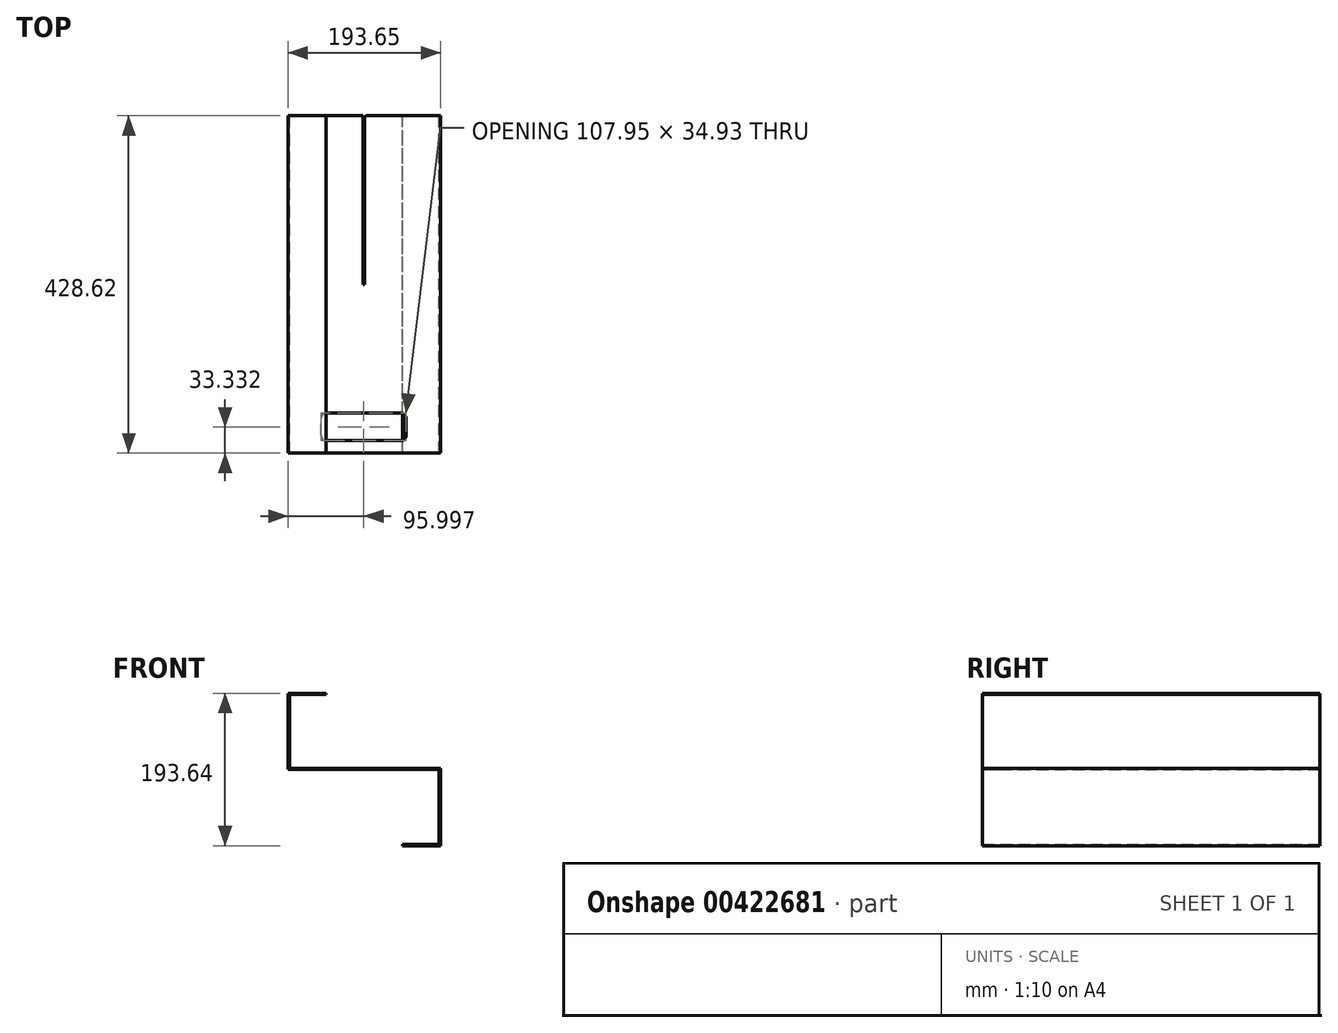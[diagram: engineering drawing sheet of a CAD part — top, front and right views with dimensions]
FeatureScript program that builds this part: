
annotation { "Feature Type Name" : "Feature", "Feature Type Description" : "" }
export const myFeature = defineFeature(function(context is Context, id is Id, definition is map)
    precondition{}
    {
        {
            var Q0;
            Q0=qCreatedBy(makeId("Front.planeOp"),FACE);
            var sketch = newSketch(context, id + "F0", { "sketchPlane" : qUnion([Q0])});
            skLineSegment(sketch, "E0", {"start": v(0, 96.82) * mm, "end": v(-48.41, 96.82) * mm});
            skLineSegment(sketch, "E1", {"start": v(-48.41, 96.82) * mm, "end": v(-48.41, 0) * mm});
            skLineSegment(sketch, "E2", {"start": v(-48.41, 0) * mm, "end": v(143.59, 0) * mm});
            skLineSegment(sketch, "E3", {"start": v(145.24, 1.65) * mm, "end": v(145.24, -96.82) * mm});
            skLineSegment(sketch, "E4", {"start": v(145.24, -96.82) * mm, "end": v(96.82, -96.82) * mm});
            skLineSegment(sketch, "E5.0", {"start": v(0, 95.17) * mm, "end": v(-46.76, 95.17) * mm});
            skLineSegment(sketch, "E6.0", {"start": v(-46.76, 95.17) * mm, "end": v(-46.76, 1.65) * mm});
            skLineSegment(sketch, "E7.0", {"start": v(-46.76, 1.65) * mm, "end": v(145.24, 1.65) * mm});
            skLineSegment(sketch, "E8.0", {"start": v(143.59, 0) * mm, "end": v(143.59, -95.17) * mm});
            skLineSegment(sketch, "E9.0", {"start": v(143.59, -95.17) * mm, "end": v(96.82, -95.17) * mm});
            skLineSegment(sketch, "E10", {"start": v(0, 96.82) * mm, "end": v(0, 95.17) * mm});
            skLineSegment(sketch, "E11", {"start": v(96.82, -95.17) * mm, "end": v(96.82, -96.82) * mm});
            skSolve(sketch);
        }
        {
            var Q0;
            Q0=makeQuery(id+"F0.imprint","IMPRINT",FACE,{"disambiguationData":[TD([[makeQuery(id+"F0.imprint","IMPRINT",EDGE,{"derivedFrom":sQuery(id+"F0.wireOp",EDGE,"E0")}),1.0]])]});
            extrude(context, id + "F1", {"entities" : qUnion([Q0]), "depth" : 428.62 * mm});
        }
        {
            var Q0;
            Q0=makeQuery(id+"F1.opExtrude","SWEPT_FACE",FACE,{"disambiguationData":[OSD([sQuery(id+"F0.wireOp",EDGE,"E2")])]});
            var sketch = newSketch(context, id + "F2", { "sketchPlane" : qUnion([Q0])});
            skLineSegment(sketch, "E12.0", {"start": v(48.48, 0) * mm, "end": v(48.48, 214.31) * mm});
            skLineSegment(sketch, "E13.0", {"start": v(46.7, 0) * mm, "end": v(46.7, 214.31) * mm});
            skLineSegment(sketch, "E14", {"start": v(46.7, 214.31) * mm, "end": v(48.48, 214.31) * mm});
            skLineSegment(sketch, "E15", {"start": v(46.7, 0) * mm, "end": v(48.48, 0) * mm});
            skPoint(sketch, "E16.endSnap0", {"position": v(47.59, 428.63) * mm});
            skLineSegment(sketch, "E17.0", {"start": v(101.56, 406.4) * mm, "end": v(101.56, 384.18) * mm});
            skLineSegment(sketch, "E18", {"start": v(-0.04, 377.83) * mm, "end": v(95.21, 377.83) * mm});
            skLineSegment(sketch, "E19.0", {"start": v(-0.04, 412.75) * mm, "end": v(95.21, 412.75) * mm});
            skLineSegment(sketch, "E20.trimOffspring", {"start": v(-6.39, 406.4) * mm, "end": v(-6.39, 384.18) * mm});
            skPoint(sketch, "E21.visualSharp", {"position": v(-6.39, 412.75) * mm});
            skArc(sketch, "E21.filletArc", {"start": v(-0.04, 412.75) * mm, "mid": v(-4.53, 410.9) * mm, "end": v(-6.39, 406.4) * mm});
            skPoint(sketch, "E22.visualSharp", {"position": v(-6.39, 377.83) * mm});
            skArc(sketch, "E22.filletArc", {"start": v(-6.39, 384.18) * mm, "mid": v(-4.53, 379.68) * mm, "end": v(-0.04, 377.83) * mm});
            skPoint(sketch, "E23.visualSharp", {"position": v(101.56, 377.83) * mm});
            skArc(sketch, "E23.filletArc", {"start": v(95.21, 377.83) * mm, "mid": v(99.7, 379.68) * mm, "end": v(101.56, 384.18) * mm});
            skPoint(sketch, "E24.visualSharp", {"position": v(101.56, 412.75) * mm});
            skArc(sketch, "E24.filletArc", {"start": v(101.56, 406.4) * mm, "mid": v(99.7, 410.9) * mm, "end": v(95.21, 412.75) * mm});
            skSolve(sketch);
        }
        {
            var Q0;
            Q0 = qSketchRegion(id + "F2", true);
            extrude(context, id + "F3", {"entities" : qUnion([Q0]), "operationType" : NewBodyOperationType.REMOVE, "oppositeDirection" : true, "depth" : 1.65 * mm});
        }
        {
            var Q0;
            Q0=makeQuery(id+"F3.boolean.opBoolean","COPY",EDGE,{"derivedFrom":makeQuery(id+"F3.opExtrude","SWEPT_EDGE",EDGE,{"disambiguationData":[OSD([sQuery(id+"F0.wireOp",EDGE,"E2"),sQuery(id+"F2.wireOp",EDGE,"E12.0"),sQuery(id+"F2.wireOp",EDGE,"E15")])]})});
            var Q1;
            Q1=makeQuery(id+"F3.boolean.opBoolean","COPY",EDGE,{"derivedFrom":makeQuery(id+"F3.opExtrude","SWEPT_EDGE",EDGE,{"disambiguationData":[OSD([sQuery(id+"F0.wireOp",EDGE,"E2"),sQuery(id+"F2.wireOp",EDGE,"E13.0"),sQuery(id+"F2.wireOp",EDGE,"E15")])]})});
            fillet(context, id + "F4", {"entities" : qUnion([Q0, Q1]), "radius" : 3.17 * mm, "tangentPropagation" : true, "allowEdgeOverflow" : false});
        }
        {
            var Q0;
            Q0=makeQuery(id+"F3.boolean.opBoolean","COPY",EDGE,{"derivedFrom":makeQuery(id+"F3.opExtrude","SWEPT_EDGE",EDGE,{"disambiguationData":[OSD([sQuery(id+"F2.wireOp",EDGE,"E13.0"),sQuery(id+"F2.wireOp",EDGE,"E14")])]})});
            var Q1;
            Q1=makeQuery(id+"F3.boolean.opBoolean","COPY",EDGE,{"derivedFrom":makeQuery(id+"F3.opExtrude","SWEPT_EDGE",EDGE,{"disambiguationData":[OSD([sQuery(id+"F2.wireOp",EDGE,"E12.0"),sQuery(id+"F2.wireOp",EDGE,"E14")])]})});
            fillet(context, id + "F5", {"entities" : qUnion([Q0, Q1]), "radius" : 0.76 * mm, "tangentPropagation" : true, "allowEdgeOverflow" : false});
        }
        {
            var Q0;
            Q0 = qSketchRegion(id + "F2", true);
            extrude(context, id + "F6", {"entities" : qUnion([Q0]), "operationType" : NewBodyOperationType.REMOVE, "oppositeDirection" : true, "depth" : 25.4 * mm});
        }
    });
